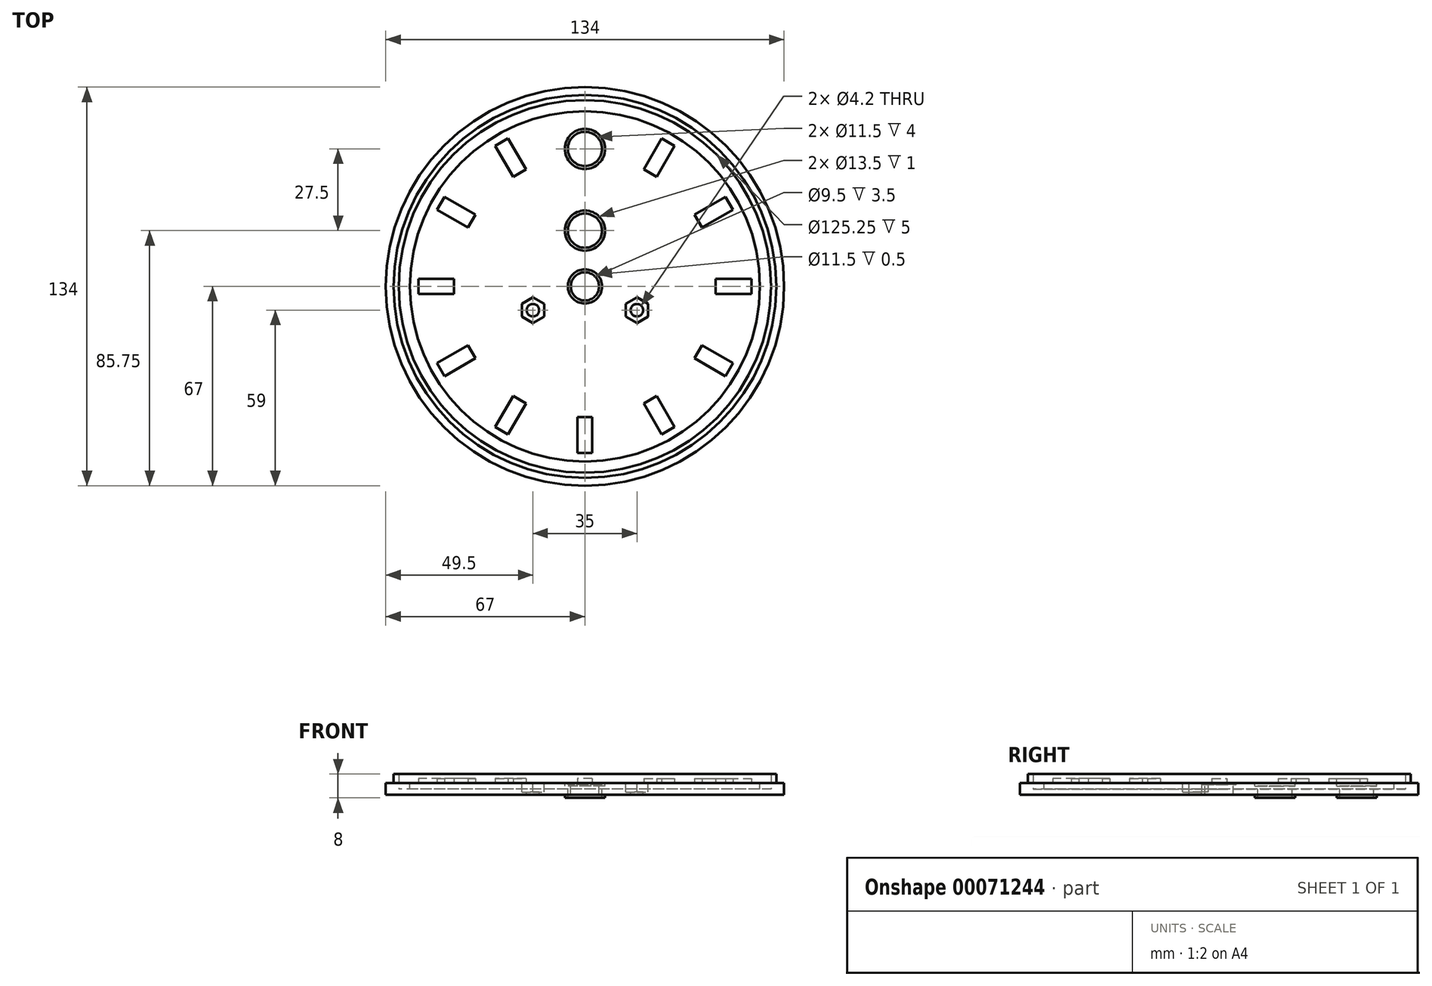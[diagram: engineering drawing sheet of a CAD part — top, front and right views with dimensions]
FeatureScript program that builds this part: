
annotation { "Feature Type Name" : "Feature", "Feature Type Description" : "" }
export const myFeature = defineFeature(function(context is Context, id is Id, definition is map)
    precondition{}
    {
        {
            var Q0;
            Q0=qCreatedBy(makeId("Top.planeOp"),FACE);
            var sketch = newSketch(context, id + "F0", { "sketchPlane" : qUnion([Q0])});
            skCircle(sketch, "E0", {"center": v(0, 0) * mm, "radius": 67 * mm});
            skSolve(sketch);
        }
        {
            var Q0;
            Q0=makeQuery(id+"F0.imprint","IMPRINT",FACE,{"disambiguationData":[TD([[makeQuery(id+"F0.imprint","IMPRINT",EDGE,{"derivedFrom":sQuery(id+"F0.wireOp",EDGE,"E0")}),1.0]])]});
            extrude(context, id + "F1", {"entities" : qUnion([Q0]), "endBound" : BoundingType.SYMMETRIC, "depth" : 5 * mm});
        }
        {
            var Q0;
            Q0=makeQuery(id+"F1.opExtrude","CAP_FACE",FACE,{"disambiguationData":[OSD([sQuery(id+"F0.wireOp",EDGE,"E0")])],"isStart":false});
            var sketch = newSketch(context, id + "F2", { "sketchPlane" : qUnion([Q0])});
            skCircle(sketch, "E1", {"center": v(0, 0) * mm, "radius": 58.88 * mm});
            skCircle(sketch, "E2", {"center": v(0, 0) * mm, "radius": 62.62 * mm});
            skCircle(sketch, "E3", {"center": v(0, 0) * mm, "radius": 64.38 * mm});
            skSolve(sketch);
        }
        {
            var Q0;
            Q0=makeQuery(id+"F2.imprint","IMPRINT",FACE,{"disambiguationData":[TD([[makeQuery(id+"F2.imprint","IMPRINT",EDGE,{"derivedFrom":sQuery(id+"F2.wireOp",EDGE,"E2")}),-1.0]])]});
            extrude(context, id + "F3", {"entities" : qUnion([Q0]), "operationType" : NewBodyOperationType.ADD, "depth" : 3 * mm});
        }
        {
            var Q0;
            Q0=makeQuery(id+"F2.imprint","IMPRINT",FACE,{"disambiguationData":[TD([[makeQuery(id+"F2.imprint","IMPRINT",EDGE,{"derivedFrom":sQuery(id+"F2.wireOp",EDGE,"E1")}),-1.0]])]});
            extrude(context, id + "F4", {"entities" : qUnion([Q0]), "operationType" : NewBodyOperationType.REMOVE, "oppositeDirection" : true, "depth" : 2 * mm});
        }
        {
            var Q0;
            Q0=makeQuery(id+"F2.imprint","IMPRINT",FACE,{"disambiguationData":[TD([[makeQuery(id+"F2.imprint","IMPRINT",EDGE,{"derivedFrom":sQuery(id+"F2.wireOp",EDGE,"E1")}),1.0]])]});
            var sketch = newSketch(context, id + "F5", { "sketchPlane" : qUnion([Q0])});
            skCircle(sketch, "E4", {"center": v(0, 0) * mm, "radius": 4.75 * mm});
            skCircle(sketch, "E5", {"center": v(0, 18.75) * mm, "radius": 5.75 * mm});
            skCircle(sketch, "E6", {"center": v(0, 46.25) * mm, "radius": 5.75 * mm});
            skLineSegment(sketch, "E7", {"start": v(0, -8) * mm, "end": v(17.5, -8) * mm, "construction": true});
            skCircle(sketch, "E8", {"center": v(17.5, -8) * mm, "radius": 2.1 * mm});
            skLineSegment(sketch, "E9", {"start": v(0, -8) * mm, "end": v(0, -2.37) * mm, "construction": true});
            skCircle(sketch, "E10.MirrorC", {"center": v(-17.5, -8) * mm, "radius": 2.1 * mm});
            skSolve(sketch);
        }
        {
            var Q0;
            Q0 = qSketchRegion(id + "F5", true);
            extrude(context, id + "F6", {"entities" : qUnion([Q0]), "operationType" : NewBodyOperationType.REMOVE, "oppositeDirection" : true, "depth" : 25 * mm});
        }
        {
            var Q0;
            Q0=makeQuery(id+"F2.imprint","IMPRINT",FACE,{"disambiguationData":[TD([[makeQuery(id+"F2.imprint","IMPRINT",EDGE,{"derivedFrom":sQuery(id+"F2.wireOp",EDGE,"E1")}),1.0]])]});
            var sketch = newSketch(context, id + "F7", { "sketchPlane" : qUnion([Q0])});
            skCircle(sketch, "E11.0", {"center": v(0, 46.25) * mm, "radius": 5.75 * mm});
            skCircle(sketch, "E12.0", {"center": v(0, 18.75) * mm, "radius": 5.75 * mm});
            skCircle(sketch, "E13.0", {"center": v(0, 0) * mm, "radius": 4.75 * mm});
            skCircle(sketch, "E14.0", {"center": v(17.5, -8) * mm, "radius": 2.1 * mm});
            skCircle(sketch, "E15.0", {"center": v(-17.5, -8) * mm, "radius": 2.1 * mm});
            skCircle(sketch, "E16", {"center": v(0, 46.25) * mm, "radius": 6.75 * mm});
            skCircle(sketch, "E17", {"center": v(0, 18.75) * mm, "radius": 6.75 * mm});
            skCircle(sketch, "E18", {"center": v(0, 0) * mm, "radius": 5.75 * mm});
            skCircle(sketch, "E19.cCircle", {"center": v(-17.5, -8) * mm, "radius": 3.75 * mm, "construction": true});
            skLineSegment(sketch, "E19.0", {"start": v(-13.75, -5.83) * mm, "end": v(-13.75, -10.17) * mm});
            skLineSegment(sketch, "E19.1", {"start": v(-13.75, -10.17) * mm, "end": v(-17.5, -12.33) * mm});
            skLineSegment(sketch, "E19.2", {"start": v(-17.5, -12.33) * mm, "end": v(-21.25, -10.17) * mm});
            skLineSegment(sketch, "E19.3", {"start": v(-21.25, -10.17) * mm, "end": v(-21.25, -5.83) * mm});
            skLineSegment(sketch, "E19.4", {"start": v(-21.25, -5.83) * mm, "end": v(-17.5, -3.67) * mm});
            skLineSegment(sketch, "E19.5", {"start": v(-17.5, -3.67) * mm, "end": v(-13.75, -5.83) * mm});
            skPoint(sketch, "E19.0.midPoint", {"position": v(-13.75, -8) * mm});
            skCircle(sketch, "E20.cCircle", {"center": v(17.5, -8) * mm, "radius": 3.75 * mm, "construction": true});
            skLineSegment(sketch, "E20.0", {"start": v(21.25, -5.83) * mm, "end": v(21.25, -10.17) * mm});
            skLineSegment(sketch, "E20.1", {"start": v(21.25, -10.17) * mm, "end": v(17.5, -12.33) * mm});
            skLineSegment(sketch, "E20.2", {"start": v(17.5, -12.33) * mm, "end": v(13.75, -10.17) * mm});
            skLineSegment(sketch, "E20.3", {"start": v(13.75, -10.17) * mm, "end": v(13.75, -5.83) * mm});
            skLineSegment(sketch, "E20.4", {"start": v(13.75, -5.83) * mm, "end": v(17.5, -3.67) * mm});
            skLineSegment(sketch, "E20.5", {"start": v(17.5, -3.67) * mm, "end": v(21.25, -5.83) * mm});
            skPoint(sketch, "E20.0.midPoint", {"position": v(21.25, -8) * mm});
            skSolve(sketch);
        }
        {
            var Q0;
            Q0=makeQuery(id+"F7.imprint","IMPRINT",FACE,{"disambiguationData":[TD([[makeQuery(id+"F7.imprint","IMPRINT",EDGE,{"derivedFrom":sQuery(id+"F7.wireOp",EDGE,"E13.0")}),-1.0]])]});
            extrude(context, id + "F8", {"entities" : qUnion([Q0]), "operationType" : NewBodyOperationType.REMOVE, "oppositeDirection" : true, "depth" : .5 * mm});
        }
        {
            var Q0;
            Q0=makeQuery(id+"F7.imprint","IMPRINT",FACE,{"disambiguationData":[TD([[makeQuery(id+"F7.imprint","IMPRINT",EDGE,{"derivedFrom":sQuery(id+"F7.wireOp",EDGE,"E12.0")}),-1.0]])]});
            var Q1;
            Q1=makeQuery(id+"F7.imprint","IMPRINT",FACE,{"disambiguationData":[TD([[makeQuery(id+"F7.imprint","IMPRINT",EDGE,{"derivedFrom":sQuery(id+"F7.wireOp",EDGE,"E11.0")}),-1.0]])]});
            extrude(context, id + "F9", {"entities" : qUnion([Q0, Q1]), "operationType" : NewBodyOperationType.REMOVE, "oppositeDirection" : true, "depth" : 1 * mm});
        }
        {
            var Q0;
            Q0=makeQuery(id+"F7.imprint","IMPRINT",FACE,{"disambiguationData":[TD([[makeQuery(id+"F7.imprint","IMPRINT",EDGE,{"derivedFrom":sQuery(id+"F7.wireOp",EDGE,"E15.0")}),-1.0]])]});
            var Q1;
            Q1=makeQuery(id+"F7.imprint","IMPRINT",FACE,{"disambiguationData":[TD([[makeQuery(id+"F7.imprint","IMPRINT",EDGE,{"derivedFrom":sQuery(id+"F7.wireOp",EDGE,"E14.0")}),-1.0]])]});
            extrude(context, id + "F10", {"entities" : qUnion([Q0, Q1]), "operationType" : NewBodyOperationType.REMOVE, "oppositeDirection" : true, "depth" : 3 * mm});
        }
        {
            var Q0;
            Q0=makeQuery(id+"F1.opExtrude","CAP_FACE",FACE,{"disambiguationData":[OSD([sQuery(id+"F0.wireOp",EDGE,"E0")])],"isStart":true});
            var sketch = newSketch(context, id + "F11", { "sketchPlane" : qUnion([Q0])});
            skCircle(sketch, "E21.0", {"center": v(0, -18.75) * mm, "radius": 6.75 * mm});
            skCircle(sketch, "E22.0", {"center": v(0, -46.25) * mm, "radius": 6.75 * mm});
            skSolve(sketch);
        }
        {
            var Q0;
            Q0=makeQuery(id+"F11.imprint","IMPRINT",FACE,{"disambiguationData":[TD([[makeQuery(id+"F11.imprint","IMPRINT",EDGE,{"derivedFrom":sQuery(id+"F11.wireOp",EDGE,"E21.0")}),-1.0]])]});
            var Q1;
            Q1=makeQuery(id+"F11.imprint","IMPRINT",FACE,{"disambiguationData":[TD([[makeQuery(id+"F11.imprint","IMPRINT",EDGE,{"derivedFrom":sQuery(id+"F11.wireOp",EDGE,"E22.0")}),-1.0]])]});
            extrude(context, id + "F12", {"entities" : qUnion([Q0, Q1]), "operationType" : NewBodyOperationType.REMOVE, "oppositeDirection" : true, "depth" : 1 * mm});
        }
        {
            var Q0;
            Q0=makeQuery(id+"F2.imprint","IMPRINT",FACE,{"disambiguationData":[TD([[makeQuery(id+"F2.imprint","IMPRINT",EDGE,{"derivedFrom":sQuery(id+"F2.wireOp",EDGE,"E1")}),1.0]])]});
            var sketch = newSketch(context, id + "F13", { "sketchPlane" : qUnion([Q0])});
            skCircle(sketch, "E23", {"center": v(0, 0) * mm, "radius": 50 * mm, "construction": true});
            skLineSegment(sketch, "E24.rect.bottom", {"start": v(2.5, -44) * mm, "end": v(-2.5, -44) * mm});
            skLineSegment(sketch, "E24.rect.top", {"start": v(2.5, -56) * mm, "end": v(-2.5, -56) * mm});
            skLineSegment(sketch, "E24.rect.left", {"start": v(2.5, -44) * mm, "end": v(2.5, -56) * mm});
            skLineSegment(sketch, "E24.rect.right", {"start": v(-2.5, -44) * mm, "end": v(-2.5, -56) * mm});
            skPoint(sketch, "E24.rect.middle", {"position": v(0, -50) * mm});
            skSolve(sketch);
        }
        {
            var Q0;
            Q0=makeQuery(id+"F13.imprint","IMPRINT",FACE,{"disambiguationData":[TD([[makeQuery(id+"F13.imprint","IMPRINT",EDGE,{"derivedFrom":sQuery(id+"F13.wireOp",EDGE,"E24.rect.bottom")}),1.0]])]});
            extrude(context, id + "F14", {"entities" : qUnion([Q0]), "operationType" : NewBodyOperationType.ADD, "depth" : 1.5 * mm});
        }
        {
            var Q0;
            Q0=makeQuery(id+"F14.opExtrude","SWEPT_FACE",FACE,{"disambiguationData":[OSD([sQuery(id+"F13.wireOp",EDGE,"E24.rect.left")])]});
            var Q1;
            Q1=makeQuery(id+"F14.opExtrude","CAP_FACE",FACE,{"disambiguationData":[OSD([sQuery(id+"F13.wireOp",EDGE,"E24.rect.bottom"),sQuery(id+"F13.wireOp",EDGE,"E24.rect.top"),sQuery(id+"F13.wireOp",EDGE,"E24.rect.left"),sQuery(id+"F13.wireOp",EDGE,"E24.rect.right")])],"isStart":false});
            var Q2;
            Q2=makeQuery(id+"F14.opExtrude","SWEPT_FACE",FACE,{"disambiguationData":[OSD([sQuery(id+"F13.wireOp",EDGE,"E24.rect.top")])]});
            var Q3;
            Q3=makeQuery(id+"F14.opExtrude","SWEPT_FACE",FACE,{"disambiguationData":[OSD([sQuery(id+"F13.wireOp",EDGE,"E24.rect.right")])]});
            var Q4;
            Q4=makeQuery(id+"F14.opExtrude","SWEPT_FACE",FACE,{"disambiguationData":[OSD([sQuery(id+"F13.wireOp",EDGE,"E24.rect.bottom")])]});
            var Q5;
            Q5=makeQuery(id+"F6.boolean.opBoolean","COPY",FACE,{"derivedFrom":makeQuery(id+"F6.opExtrude","SWEPT_FACE",FACE,{"disambiguationData":[OSD([sQuery(id+"F5.wireOp",EDGE,"E4")])]})});
            circularPattern(context, id + "F15", {"faces" : qUnion([Q0, Q1, Q2, Q3, Q4]), "axis" : qUnion([Q5]), "angle" : 30 * degree, "instanceCount" : 6, "oppositeDirection" : true, "patternType" : PatternType.FACE});
        }
        {
            var Q0;
            Q0=makeQuery(id+"F14.opExtrude","SWEPT_FACE",FACE,{"disambiguationData":[OSD([sQuery(id+"F13.wireOp",EDGE,"E24.rect.left")])]});
            var Q1;
            Q1=makeQuery(id+"F14.opExtrude","CAP_FACE",FACE,{"disambiguationData":[OSD([sQuery(id+"F13.wireOp",EDGE,"E24.rect.bottom"),sQuery(id+"F13.wireOp",EDGE,"E24.rect.top"),sQuery(id+"F13.wireOp",EDGE,"E24.rect.left"),sQuery(id+"F13.wireOp",EDGE,"E24.rect.right")])],"isStart":false});
            var Q2;
            Q2=makeQuery(id+"F14.opExtrude","SWEPT_FACE",FACE,{"disambiguationData":[OSD([sQuery(id+"F13.wireOp",EDGE,"E24.rect.top")])]});
            var Q3;
            Q3=makeQuery(id+"F14.opExtrude","SWEPT_FACE",FACE,{"disambiguationData":[OSD([sQuery(id+"F13.wireOp",EDGE,"E24.rect.bottom")])]});
            var Q4;
            Q4=makeQuery(id+"F14.opExtrude","SWEPT_FACE",FACE,{"disambiguationData":[OSD([sQuery(id+"F13.wireOp",EDGE,"E24.rect.right")])]});
            var Q5;
            Q5=makeQuery(id+"F6.boolean.opBoolean","COPY",FACE,{"derivedFrom":makeQuery(id+"F6.opExtrude","SWEPT_FACE",FACE,{"disambiguationData":[OSD([sQuery(id+"F5.wireOp",EDGE,"E4")])]})});
            circularPattern(context, id + "F16", {"faces" : qUnion([Q0, Q1, Q2, Q3, Q4]), "axis" : qUnion([Q5]), "angle" : 30 * degree, "instanceCount" : 6, "patternType" : PatternType.FACE});
        }
    });
